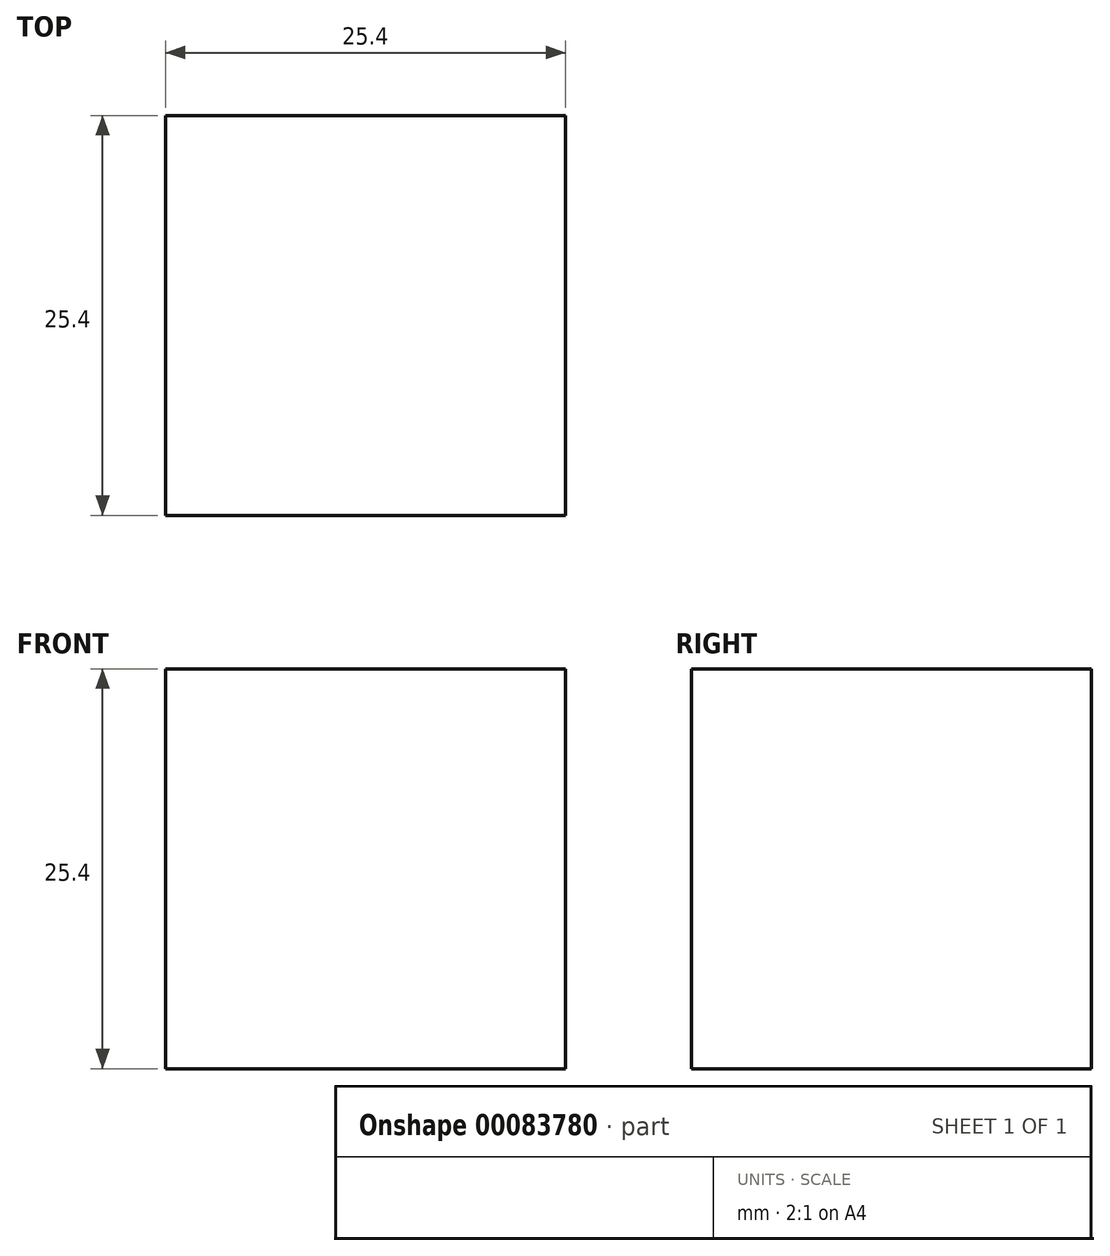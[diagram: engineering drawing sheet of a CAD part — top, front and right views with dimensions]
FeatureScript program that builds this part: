
annotation { "Feature Type Name" : "Feature", "Feature Type Description" : "" }
export const myFeature = defineFeature(function(context is Context, id is Id, definition is map)
    precondition{}
    {
        {
            var Q0;
            Q0=qCreatedBy(makeId("Top.planeOp"),FACE);
            var sketch = newSketch(context, id + "F0", { "sketchPlane" : qUnion([Q0])});
            skLineSegment(sketch, "E0.bottom", {"start": v(12.7, 12.7) * mm, "end": v(-12.7, 12.7) * mm});
            skLineSegment(sketch, "E0.top", {"start": v(12.7, -12.7) * mm, "end": v(-12.7, -12.7) * mm});
            skLineSegment(sketch, "E0.left", {"start": v(12.7, 12.7) * mm, "end": v(12.7, -12.7) * mm});
            skLineSegment(sketch, "E0.right", {"start": v(-12.7, 12.7) * mm, "end": v(-12.7, -12.7) * mm});
            skPoint(sketch, "E0.middle", {"position": v(0, 0) * mm});
            skSolve(sketch);
        }
        {
            var Q0;
            Q0 = qSketchRegion(id + "F0", true);
            extrude(context, id + "F1", {"entities" : qUnion([Q0]), "endBound" : BoundingType.SYMMETRIC, "depth" : 25.4 * mm});
        }
    });
